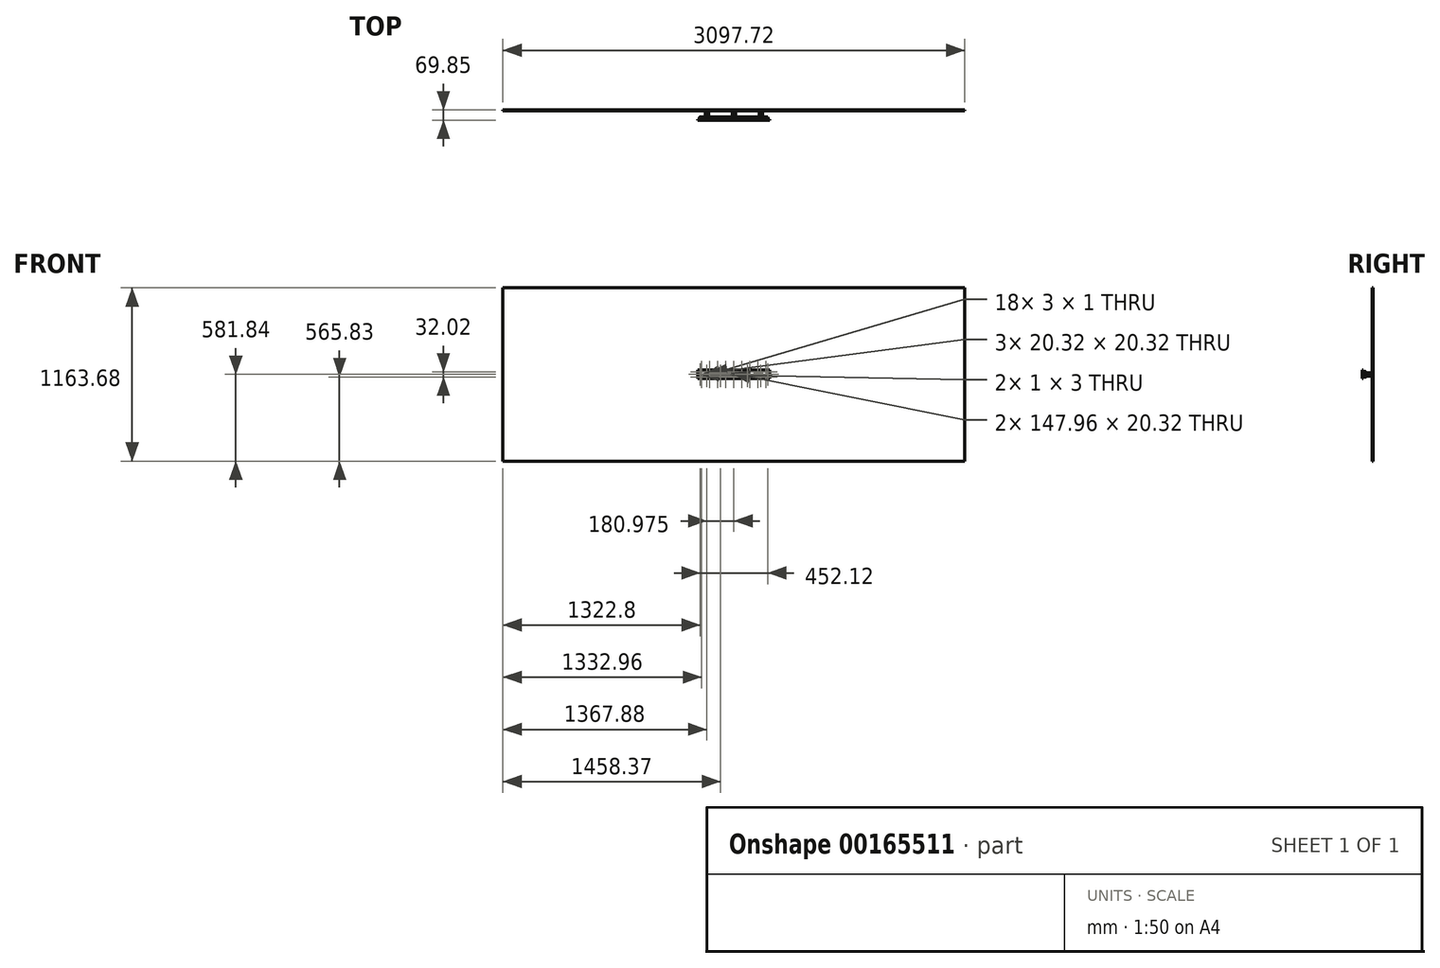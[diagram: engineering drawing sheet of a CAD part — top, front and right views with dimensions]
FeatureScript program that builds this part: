
annotation { "Feature Type Name" : "Feature", "Feature Type Description" : "" }
export const myFeature = defineFeature(function(context is Context, id is Id, definition is map)
    precondition{}
    {
        {
            var Q0;
            Q0=qCreatedBy(makeId("Front.planeOp"),FACE);
            var sketch = newSketch(context, id + "F0", { "sketchPlane" : qUnion([Q0])});
            skLineSegment(sketch, "E0.bottom", {"start": v(10.16, -10.16) * mm, "end": v(-10.16, -10.16) * mm});
            skLineSegment(sketch, "E0.top", {"start": v(10.16, 10.16) * mm, "end": v(-10.16, 10.16) * mm});
            skLineSegment(sketch, "E0.left", {"start": v(10.16, -10.16) * mm, "end": v(10.16, 10.16) * mm});
            skLineSegment(sketch, "E0.right", {"start": v(-10.16, -10.16) * mm, "end": v(-10.16, 10.16) * mm});
            skPoint(sketch, "E0.middle", {"position": v(0, 0) * mm});
            skLineSegment(sketch, "E1.1.0.0", {"start": v(191.14, 10.16) * mm, "end": v(170.82, 10.16) * mm});
            skLineSegment(sketch, "E1.1.0.1", {"start": v(170.82, -10.16) * mm, "end": v(170.82, 10.16) * mm});
            skLineSegment(sketch, "E1.1.0.2", {"start": v(191.14, -10.16) * mm, "end": v(170.82, -10.16) * mm});
            skLineSegment(sketch, "E1.1.0.3", {"start": v(191.14, -10.16) * mm, "end": v(191.14, 10.16) * mm});
            skLineSegment(sketch, "E1.direction1", {"start": v(-10.16, 10.16) * mm, "end": v(170.82, 10.16) * mm, "construction": true});
            skLineSegment(sketch, "E2.MirrorCS", {"start": v(-170.82, -10.16) * mm, "end": v(-170.82, 10.16) * mm});
            skLineSegment(sketch, "E3.MirrorCS", {"start": v(-191.14, 10.16) * mm, "end": v(-170.82, 10.16) * mm});
            skLineSegment(sketch, "E4.MirrorCS", {"start": v(-191.14, -10.16) * mm, "end": v(-170.82, -10.16) * mm});
            skLineSegment(sketch, "E5.MirrorCS", {"start": v(-191.14, -10.16) * mm, "end": v(-191.14, 10.16) * mm});
            skSolve(sketch);
        }
        {
            var Q0;
            Q0=qSketchRegion(id+"F0",true);
            extrude(context, id + "F1", {"entities" : qUnion([Q0]), "depth" : 63.5 * mm});
        }
        {
            var Q0;
            Q0=makeQuery(id+"F1.opExtrude","CAP_FACE",FACE,{"disambiguationData":[OSD([sQuery(id+"F0.wireOp",EDGE,"E2.MirrorCS"),sQuery(id+"F0.wireOp",EDGE,"E3.MirrorCS"),sQuery(id+"F0.wireOp",EDGE,"E4.MirrorCS"),sQuery(id+"F0.wireOp",EDGE,"E5.MirrorCS")])],"isStart":false});
            var sketch = newSketch(context, id + "F2", { "sketchPlane" : qUnion([Q0])});
            skLineSegment(sketch, "E6.bottom", {"start": v(241.3, -28.57) * mm, "end": v(-241.3, -28.58) * mm});
            skLineSegment(sketch, "E6.top", {"start": v(241.3, 28.58) * mm, "end": v(-241.3, 28.57) * mm});
            skLineSegment(sketch, "E6.left", {"start": v(241.3, -28.57) * mm, "end": v(241.3, 28.58) * mm});
            skLineSegment(sketch, "E6.right", {"start": v(-241.3, -28.58) * mm, "end": v(-241.3, 28.57) * mm});
            skPoint(sketch, "E6.middle", {"position": v(0, 0) * mm});
            skSolve(sketch);
        }
        {
            var Q0;
            Q0=qSketchRegion(id+"F2",true);
            extrude(context, id + "F3", {"entities" : qUnion([Q0]), "depth" : 6.35 * mm});
        }
        {
            var Q0;
            Q0=makeQuery(id+"F3.opExtrude","CAP_FACE",FACE,{"disambiguationData":[OSD([sQuery(id+"F2.wireOp",EDGE,"E6.bottom"),sQuery(id+"F2.wireOp",EDGE,"E6.top"),sQuery(id+"F2.wireOp",EDGE,"E6.left"),sQuery(id+"F2.wireOp",EDGE,"E6.right")])],"isStart":true});
            cPlane(context, id + "F4", {"entities" : qUnion([Q0]), "cplaneType" : CPlaneType.OFFSET, "offset" : 3 * mm, "width" : 152.4 * mm, "height" : 152.4 * mm});
        }
        {
            var Q0;
            Q0=qCreatedBy(id+"F4.planeOp",FACE);
            var sketch = newSketch(context, id + "F5", { "sketchPlane" : qUnion([Q0])});
            skLineSegment(sketch, "E7.bottom", {"start": v(228.6, -19.05) * mm, "end": v(-228.6, -19.05) * mm});
            skLineSegment(sketch, "E7.top", {"start": v(228.6, 19.05) * mm, "end": v(-228.6, 19.05) * mm});
            skLineSegment(sketch, "E7.left", {"start": v(228.6, -19.05) * mm, "end": v(228.6, 19.05) * mm});
            skLineSegment(sketch, "E7.right", {"start": v(-228.6, -19.05) * mm, "end": v(-228.6, 19.05) * mm});
            skPoint(sketch, "E7.middle", {"position": v(0, 0) * mm});
            skLineSegment(sketch, "E8.1", {"start": v(-191.14, 10.16) * mm, "end": v(-170.82, 10.16) * mm});
            skLineSegment(sketch, "E8.2", {"start": v(-191.14, -10.16) * mm, "end": v(-191.14, 10.16) * mm});
            skLineSegment(sketch, "E8.3", {"start": v(-191.14, -10.16) * mm, "end": v(-170.82, -10.16) * mm});
            skLineSegment(sketch, "E8.4", {"start": v(-170.82, -10.16) * mm, "end": v(-170.82, 10.16) * mm});
            skLineSegment(sketch, "E8.5", {"start": v(-10.16, -10.16) * mm, "end": v(-10.16, 10.16) * mm});
            skLineSegment(sketch, "E8.6", {"start": v(-10.16, 10.16) * mm, "end": v(10.16, 10.16) * mm});
            skLineSegment(sketch, "E8.7", {"start": v(10.16, -10.16) * mm, "end": v(10.16, 10.16) * mm});
            skLineSegment(sketch, "E8.8", {"start": v(-10.16, -10.16) * mm, "end": v(10.16, -10.16) * mm});
            skLineSegment(sketch, "E8.9", {"start": v(191.14, 10.16) * mm, "end": v(170.82, 10.16) * mm});
            skLineSegment(sketch, "E8.10", {"start": v(170.82, -10.16) * mm, "end": v(170.82, 10.16) * mm});
            skLineSegment(sketch, "E8.11", {"start": v(191.14, -10.16) * mm, "end": v(170.82, -10.16) * mm});
            skLineSegment(sketch, "E8.12", {"start": v(191.14, -10.16) * mm, "end": v(191.14, 10.16) * mm});
            skLineSegment(sketch, "E9", {"start": v(0, 19.05) * mm, "end": v(0, 10.16) * mm, "construction": true});
            skLineSegment(sketch, "E10.bottom", {"start": v(1.5, 15.51) * mm, "end": v(-1.5, 15.51) * mm});
            skLineSegment(sketch, "E10.top", {"start": v(1.5, 16.51) * mm, "end": v(-1.5, 16.51) * mm});
            skLineSegment(sketch, "E10.left", {"start": v(1.5, 15.51) * mm, "end": v(1.5, 16.51) * mm});
            skLineSegment(sketch, "E10.right", {"start": v(-1.5, 15.51) * mm, "end": v(-1.5, 16.5) * mm});
            skPoint(sketch, "E10.middle", {"position": v(0, 14.6) * mm});
            skLineSegment(sketch, "E11.1.0.0", {"start": v(55.47, 16.51) * mm, "end": v(52.48, 16.51) * mm});
            skLineSegment(sketch, "E11.1.0.1", {"start": v(52.47, 15.51) * mm, "end": v(52.47, 16.51) * mm});
            skLineSegment(sketch, "E11.1.0.2", {"start": v(55.47, 15.51) * mm, "end": v(52.48, 15.51) * mm});
            skLineSegment(sketch, "E11.1.0.3", {"start": v(55.47, 15.51) * mm, "end": v(55.47, 16.51) * mm});
            skLineSegment(sketch, "E11.2.0.0", {"start": v(109.45, 16.51) * mm, "end": v(106.45, 16.51) * mm});
            skLineSegment(sketch, "E11.2.0.1", {"start": v(106.45, 15.51) * mm, "end": v(106.45, 16.51) * mm});
            skLineSegment(sketch, "E11.2.0.2", {"start": v(109.45, 15.51) * mm, "end": v(106.45, 15.51) * mm});
            skLineSegment(sketch, "E11.2.0.3", {"start": v(109.45, 15.51) * mm, "end": v(109.45, 16.51) * mm});
            skLineSegment(sketch, "E11.3.0.0", {"start": v(163.43, 16.51) * mm, "end": v(160.43, 16.51) * mm});
            skLineSegment(sketch, "E11.3.0.1", {"start": v(160.43, 15.51) * mm, "end": v(160.43, 16.51) * mm});
            skLineSegment(sketch, "E11.3.0.2", {"start": v(163.43, 15.51) * mm, "end": v(160.43, 15.51) * mm});
            skLineSegment(sketch, "E11.3.0.3", {"start": v(163.43, 15.51) * mm, "end": v(163.43, 16.51) * mm});
            skLineSegment(sketch, "E11.direction1", {"start": v(-1.5, 16.51) * mm, "end": v(52.48, 16.51) * mm, "construction": true});
            skLineSegment(sketch, "E12.MirrorCS", {"start": v(-52.47, 15.51) * mm, "end": v(-52.47, 16.51) * mm});
            skLineSegment(sketch, "E13.MirrorCS", {"start": v(-55.47, 15.51) * mm, "end": v(-55.47, 16.51) * mm});
            skLineSegment(sketch, "E14.MirrorCS", {"start": v(-109.45, 16.51) * mm, "end": v(-106.45, 16.51) * mm});
            skLineSegment(sketch, "E15.MirrorCS", {"start": v(-160.43, 15.51) * mm, "end": v(-160.43, 16.51) * mm});
            skLineSegment(sketch, "E16.MirrorCS", {"start": v(-55.47, 16.51) * mm, "end": v(-52.48, 16.51) * mm});
            skLineSegment(sketch, "E17.MirrorCS", {"start": v(-109.45, 15.51) * mm, "end": v(-109.45, 16.51) * mm});
            skLineSegment(sketch, "E18.MirrorCS", {"start": v(-163.43, 15.51) * mm, "end": v(-163.43, 16.51) * mm});
            skLineSegment(sketch, "E19.MirrorCS", {"start": v(-106.45, 15.51) * mm, "end": v(-106.45, 16.51) * mm});
            skLineSegment(sketch, "E20.MirrorCS", {"start": v(-55.47, 15.51) * mm, "end": v(-52.48, 15.51) * mm});
            skLineSegment(sketch, "E21.MirrorCS", {"start": v(-109.45, 15.5) * mm, "end": v(-106.45, 15.5) * mm});
            skLineSegment(sketch, "E22.MirrorCS", {"start": v(-163.43, 15.5) * mm, "end": v(-160.43, 15.5) * mm});
            skLineSegment(sketch, "E23.MirrorCS", {"start": v(-163.43, 16.5) * mm, "end": v(-160.43, 16.5) * mm});
            skLineSegment(sketch, "E24.MirrorCS", {"start": v(-1.5, -15.51) * mm, "end": v(-1.5, -16.5) * mm});
            skLineSegment(sketch, "E25.MirrorCS", {"start": v(55.47, -15.51) * mm, "end": v(55.47, -16.51) * mm});
            skLineSegment(sketch, "E26.MirrorCS", {"start": v(-55.47, -16.5) * mm, "end": v(-52.48, -16.5) * mm});
            skLineSegment(sketch, "E27.MirrorCS", {"start": v(163.43, -15.5) * mm, "end": v(160.43, -15.5) * mm});
            skLineSegment(sketch, "E28.MirrorCS", {"start": v(52.48, -15.51) * mm, "end": v(52.48, -16.51) * mm});
            skLineSegment(sketch, "E29.MirrorCS", {"start": v(-52.47, -15.51) * mm, "end": v(-52.47, -16.51) * mm});
            skLineSegment(sketch, "E30.MirrorCS", {"start": v(1.5, -16.51) * mm, "end": v(-1.5, -16.51) * mm});
            skLineSegment(sketch, "E31.MirrorCS", {"start": v(-55.47, -15.5) * mm, "end": v(-52.48, -15.5) * mm});
            skLineSegment(sketch, "E32.MirrorCS", {"start": v(-55.47, -15.51) * mm, "end": v(-55.47, -16.51) * mm});
            skLineSegment(sketch, "E33.MirrorCS", {"start": v(1.5, -15.51) * mm, "end": v(1.5, -16.51) * mm});
            skLineSegment(sketch, "E34.MirrorCS", {"start": v(163.43, -15.51) * mm, "end": v(163.43, -16.51) * mm});
            skLineSegment(sketch, "E35.MirrorCS", {"start": v(163.43, -16.5) * mm, "end": v(160.43, -16.5) * mm});
            skLineSegment(sketch, "E36.MirrorCS", {"start": v(-163.43, -15.5) * mm, "end": v(-160.43, -15.5) * mm});
            skLineSegment(sketch, "E37.MirrorCS", {"start": v(109.45, -15.51) * mm, "end": v(109.45, -16.51) * mm});
            skLineSegment(sketch, "E38.MirrorCS", {"start": v(160.43, -15.51) * mm, "end": v(160.43, -16.51) * mm});
            skLineSegment(sketch, "E39.MirrorCS", {"start": v(1.5, -15.51) * mm, "end": v(-1.5, -15.51) * mm});
            skLineSegment(sketch, "E40.MirrorCS", {"start": v(106.45, -15.51) * mm, "end": v(106.45, -16.51) * mm});
            skLineSegment(sketch, "E41.MirrorCS", {"start": v(-160.43, -15.51) * mm, "end": v(-160.43, -16.51) * mm});
            skLineSegment(sketch, "E42.MirrorCS", {"start": v(-109.45, -16.5) * mm, "end": v(-106.45, -16.5) * mm});
            skLineSegment(sketch, "E43.MirrorCS", {"start": v(-106.45, -15.51) * mm, "end": v(-106.45, -16.51) * mm});
            skLineSegment(sketch, "E44.MirrorCS", {"start": v(-163.43, -15.51) * mm, "end": v(-163.43, -16.51) * mm});
            skLineSegment(sketch, "E45.MirrorCS", {"start": v(-109.45, -15.5) * mm, "end": v(-106.45, -15.5) * mm});
            skLineSegment(sketch, "E46.MirrorCS", {"start": v(-163.43, -16.5) * mm, "end": v(-160.43, -16.5) * mm});
            skLineSegment(sketch, "E47.MirrorCS", {"start": v(-109.45, -15.51) * mm, "end": v(-109.45, -16.51) * mm});
            skLineSegment(sketch, "E48.MirrorCS", {"start": v(55.47, -16.5) * mm, "end": v(52.48, -16.5) * mm});
            skPoint(sketch, "E49.MirrorP", {"position": v(0, -14.6) * mm});
            skLineSegment(sketch, "E50.MirrorCS", {"start": v(-1.5, -16.5) * mm, "end": v(52.48, -16.5) * mm, "construction": true});
            skLineSegment(sketch, "E51.MirrorCS", {"start": v(109.45, -16.5) * mm, "end": v(106.45, -16.5) * mm});
            skLineSegment(sketch, "E52.MirrorCS", {"start": v(109.45, -15.5) * mm, "end": v(106.45, -15.5) * mm});
            skLineSegment(sketch, "E53.MirrorCS", {"start": v(55.47, -15.5) * mm, "end": v(52.48, -15.5) * mm});
            skLineSegment(sketch, "E54.0", {"start": v(-241.3, -28.57) * mm, "end": v(241.3, -28.58) * mm, "construction": true});
            skLineSegment(sketch, "E54.1", {"start": v(241.3, -28.58) * mm, "end": v(241.3, 28.57) * mm, "construction": true});
            skLineSegment(sketch, "E54.2", {"start": v(-241.3, 28.58) * mm, "end": v(241.3, 28.57) * mm, "construction": true});
            skLineSegment(sketch, "E54.3", {"start": v(-241.3, -28.57) * mm, "end": v(-241.3, 28.58) * mm, "construction": true});
            skLineSegment(sketch, "E55.0.4.0", {"start": v(217.4, 16.51) * mm, "end": v(214.4, 16.51) * mm});
            skLineSegment(sketch, "E55.3.4.0", {"start": v(214.4, 15.51) * mm, "end": v(214.4, 16.51) * mm});
            skLineSegment(sketch, "E55.6.4.0", {"start": v(217.4, 15.5) * mm, "end": v(214.4, 15.5) * mm});
            skLineSegment(sketch, "E55.9.4.0", {"start": v(217.4, 15.51) * mm, "end": v(217.4, 16.51) * mm});
            skLineSegment(sketch, "E56.MirrorCS", {"start": v(-217.4, 15.51) * mm, "end": v(-217.4, 16.51) * mm});
            skLineSegment(sketch, "E57.MirrorCS", {"start": v(-214.4, 15.51) * mm, "end": v(-214.4, 16.51) * mm});
            skLineSegment(sketch, "E58.MirrorCS", {"start": v(-217.4, 15.5) * mm, "end": v(-214.4, 15.5) * mm});
            skLineSegment(sketch, "E59.MirrorCS", {"start": v(-217.4, 16.51) * mm, "end": v(-214.4, 16.51) * mm});
            skLineSegment(sketch, "E60.MirrorCS", {"start": v(214.4, -15.51) * mm, "end": v(214.4, -16.51) * mm});
            skLineSegment(sketch, "E61.MirrorCS", {"start": v(217.4, -15.5) * mm, "end": v(214.4, -15.5) * mm});
            skLineSegment(sketch, "E62.MirrorCS", {"start": v(217.4, -15.51) * mm, "end": v(217.4, -16.51) * mm});
            skLineSegment(sketch, "E63.MirrorCS", {"start": v(217.4, -16.51) * mm, "end": v(214.4, -16.51) * mm});
            skLineSegment(sketch, "E64.MirrorCS", {"start": v(-214.4, -15.51) * mm, "end": v(-214.4, -16.51) * mm});
            skLineSegment(sketch, "E65.MirrorCS", {"start": v(-217.4, -15.51) * mm, "end": v(-217.4, -16.51) * mm});
            skLineSegment(sketch, "E66.MirrorCS", {"start": v(-217.4, -16.51) * mm, "end": v(-214.4, -16.51) * mm});
            skLineSegment(sketch, "E67.MirrorCS", {"start": v(-217.4, -15.5) * mm, "end": v(-214.4, -15.5) * mm});
            skLineSegment(sketch, "E68", {"start": v(-226.06, -19.05) * mm, "end": v(-226.06, 19.05) * mm, "construction": true});
            skLineSegment(sketch, "E69.bottom", {"start": v(-226.56, 1.5) * mm, "end": v(-225.56, 1.5) * mm});
            skLineSegment(sketch, "E69.top", {"start": v(-226.56, -1.5) * mm, "end": v(-225.56, -1.5) * mm});
            skLineSegment(sketch, "E69.left", {"start": v(-226.56, 1.5) * mm, "end": v(-226.56, -1.5) * mm});
            skLineSegment(sketch, "E69.right", {"start": v(-225.56, 1.5) * mm, "end": v(-225.56, -1.5) * mm});
            skPoint(sketch, "E69.middle", {"position": v(-226.06, 0) * mm});
            skLineSegment(sketch, "E70.MirrorCS", {"start": v(226.56, -1.5) * mm, "end": v(225.56, -1.5) * mm});
            skLineSegment(sketch, "E71.MirrorCS", {"start": v(225.56, 1.5) * mm, "end": v(225.56, -1.5) * mm});
            skPoint(sketch, "E72.MirrorP", {"position": v(226.06, 0) * mm});
            skLineSegment(sketch, "E73.MirrorCS", {"start": v(226.56, 1.5) * mm, "end": v(226.56, -1.5) * mm});
            skLineSegment(sketch, "E74.MirrorCS", {"start": v(226.56, 1.5) * mm, "end": v(225.56, 1.5) * mm});
            skLineSegment(sketch, "E75.bottom", {"start": v(16.51, 10.16) * mm, "end": v(164.47, 10.16) * mm});
            skLineSegment(sketch, "E75.top", {"start": v(16.51, -10.16) * mm, "end": v(164.47, -10.16) * mm});
            skLineSegment(sketch, "E75.left", {"start": v(16.51, 10.16) * mm, "end": v(16.51, -10.16) * mm});
            skLineSegment(sketch, "E75.right", {"start": v(164.47, 10.16) * mm, "end": v(164.47, -10.16) * mm});
            skPoint(sketch, "E75.middle", {"position": v(90.49, 0) * mm});
            skLineSegment(sketch, "E76.MirrorCS", {"start": v(-16.51, -10.16) * mm, "end": v(-164.47, -10.16) * mm});
            skLineSegment(sketch, "E77.MirrorCS", {"start": v(-164.47, 10.16) * mm, "end": v(-164.47, -10.16) * mm});
            skLineSegment(sketch, "E78.MirrorCS", {"start": v(-16.51, 10.16) * mm, "end": v(-164.47, 10.16) * mm});
            skLineSegment(sketch, "E79.MirrorCS", {"start": v(-16.51, 10.16) * mm, "end": v(-16.51, -10.16) * mm});
            skSolve(sketch);
        }
        {
            var Q0;
            Q0=qSketchRegion(id+"F5",true);
            extrude(context, id + "F6", {"entities" : qUnion([Q0]), "depth" : 12.7 * mm});
        }
        {
            var Q0;
            Q0=makeQuery(id+"F6.opExtrude","SWEPT_EDGE",EDGE,{"disambiguationData":[OSD([sQuery(id+"F5.wireOp",EDGE,"E7.top"),sQuery(id+"F5.wireOp",EDGE,"E7.right")])]});
            var Q1;
            Q1=makeQuery(id+"F6.opExtrude","SWEPT_EDGE",EDGE,{"disambiguationData":[OSD([sQuery(id+"F5.wireOp",EDGE,"E7.bottom"),sQuery(id+"F5.wireOp",EDGE,"E7.right")])]});
            var Q2;
            Q2=makeQuery(id+"F6.opExtrude","SWEPT_EDGE",EDGE,{"disambiguationData":[OSD([sQuery(id+"F5.wireOp",EDGE,"E7.top"),sQuery(id+"F5.wireOp",EDGE,"E7.left")])]});
            var Q3;
            Q3=makeQuery(id+"F6.opExtrude","SWEPT_EDGE",EDGE,{"disambiguationData":[OSD([sQuery(id+"F5.wireOp",EDGE,"E7.bottom"),sQuery(id+"F5.wireOp",EDGE,"E7.left")])]});
            fillet(context, id + "F7", {"entities" : qUnion([Q0, Q1, Q2, Q3]), "radius" : 12.7 * mm, "tangentPropagation" : true, "allowEdgeOverflow" : false});
        }
        {
            var Q0;
            Q0=qCreatedBy(makeId("Front.planeOp"),FACE);
            var sketch = newSketch(context, id + "F8", { "sketchPlane" : qUnion([Q0])});
            skLineSegment(sketch, "E80.bottom", {"start": v(-1548.86, -581.84) * mm, "end": v(1548.86, -581.84) * mm});
            skLineSegment(sketch, "E80.top", {"start": v(-1548.86, 581.84) * mm, "end": v(1548.86, 581.84) * mm});
            skLineSegment(sketch, "E80.left", {"start": v(-1548.86, -581.84) * mm, "end": v(-1548.86, 581.84) * mm});
            skLineSegment(sketch, "E80.right", {"start": v(1548.86, -581.84) * mm, "end": v(1548.86, 581.84) * mm});
            skPoint(sketch, "E80.middle", {"position": v(0, 0) * mm});
            skSolve(sketch);
        }
        {
            var Q0;
            Q0=qSketchRegion(id+"F8",true);
            extrude(context, id + "F9", {"entities" : qUnion([Q0]), "depth" : 6.35 * mm});
        }
    });
